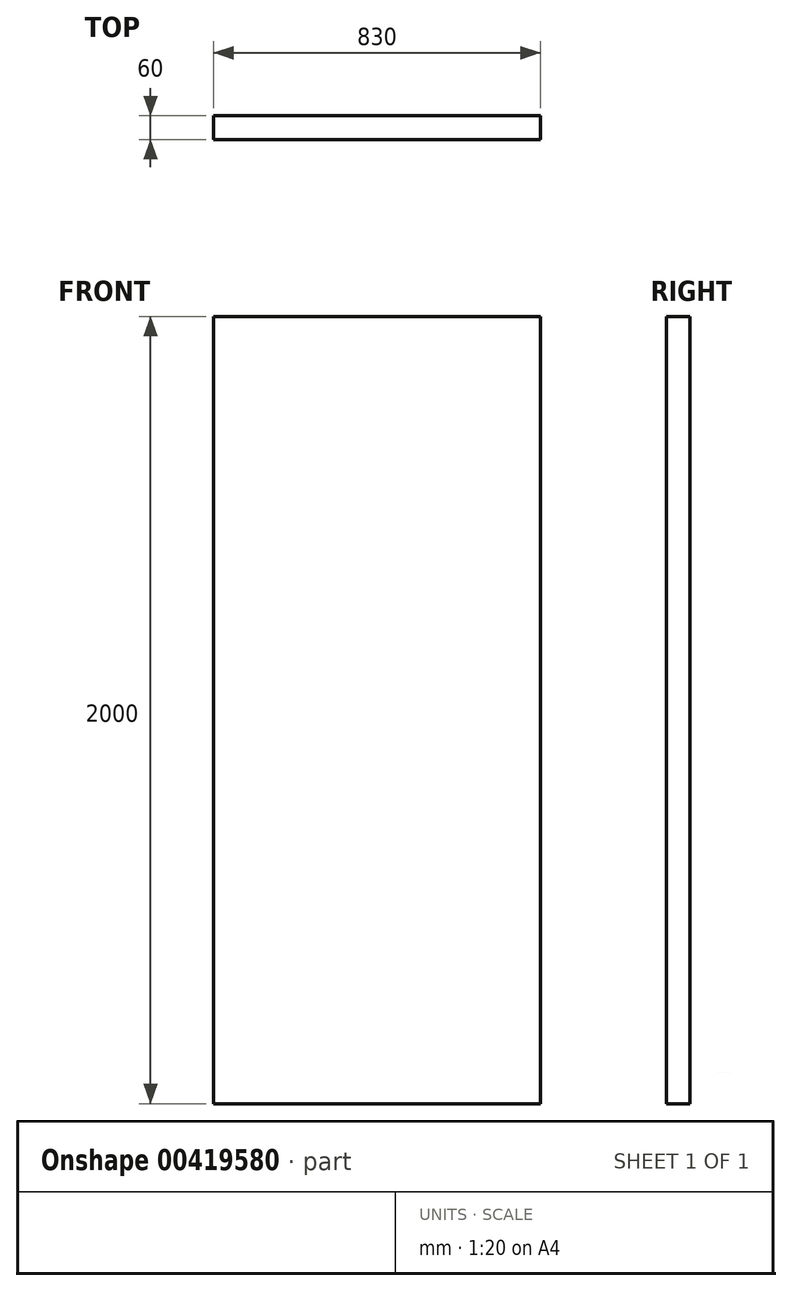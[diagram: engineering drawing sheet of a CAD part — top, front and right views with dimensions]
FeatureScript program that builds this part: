
annotation { "Feature Type Name" : "Feature", "Feature Type Description" : "" }
export const myFeature = defineFeature(function(context is Context, id is Id, definition is map)
    precondition{}
    {
        {
            var Q0;
            Q0=qCreatedBy(makeId("Top.planeOp"),FACE);
            var sketch = newSketch(context, id + "F0", { "sketchPlane" : qUnion([Q0])});
            skLineSegment(sketch, "E0.bottom", {"start": v(-418.68, -58.6) * mm, "end": v(411.32, -58.6) * mm});
            skLineSegment(sketch, "E0.top", {"start": v(-418.68, -118.6) * mm, "end": v(411.32, -118.6) * mm});
            skLineSegment(sketch, "E0.left", {"start": v(-418.68, -58.6) * mm, "end": v(-418.68, -118.6) * mm});
            skLineSegment(sketch, "E0.right", {"start": v(411.32, -58.6) * mm, "end": v(411.32, -118.6) * mm});
            skSolve(sketch);
        }
        {
            var Q0;
            Q0=makeQuery(id+"F0.imprint","IMPRINT",FACE,{"disambiguationData":[TD([[makeQuery(id+"F0.imprint","IMPRINT",EDGE,{"derivedFrom":sQuery(id+"F0.wireOp",EDGE,"E0.bottom")}),-1.0]])]});
            extrude(context, id + "F1", {"entities" : qUnion([Q0]), "depth" : 2000 * mm});
        }
    });
